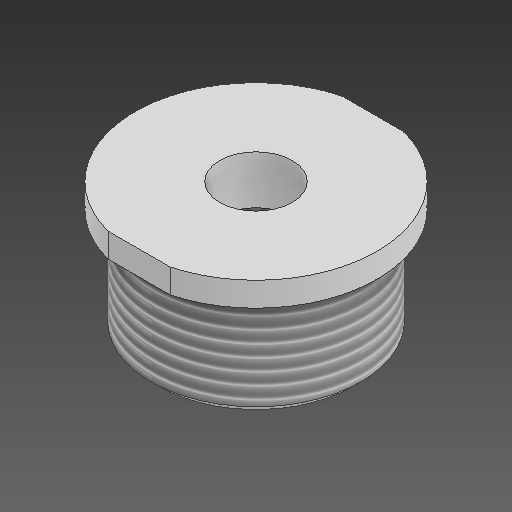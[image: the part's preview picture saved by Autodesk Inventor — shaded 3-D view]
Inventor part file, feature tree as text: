
AUTODESK INVENTOR PART (.ipt)
format: ipt  version: 2021 (Build 250183000, 183)  size: 161,280 bytes
history: native  units: in
note: dims shown in document units (in); Inventor stores cm internally (conversion verified against a paired STEP export)
features: other x3, sketch x2
ambient origin geometry x8: Origin, YZ Plane, XZ Plane, XY Plane, X Axis, Y Axis, Z Axis, Center Point
bodies: Solid1 (feature_tree)
feature tree (5):
  other  "endcap.ipt"
  other  "Solid1::endcap.ipt"
  other  "TaggingFeature1"
  sketch  "Sketch1"  dims[d0=0.3937in]
  sketch  "Sketch2"
